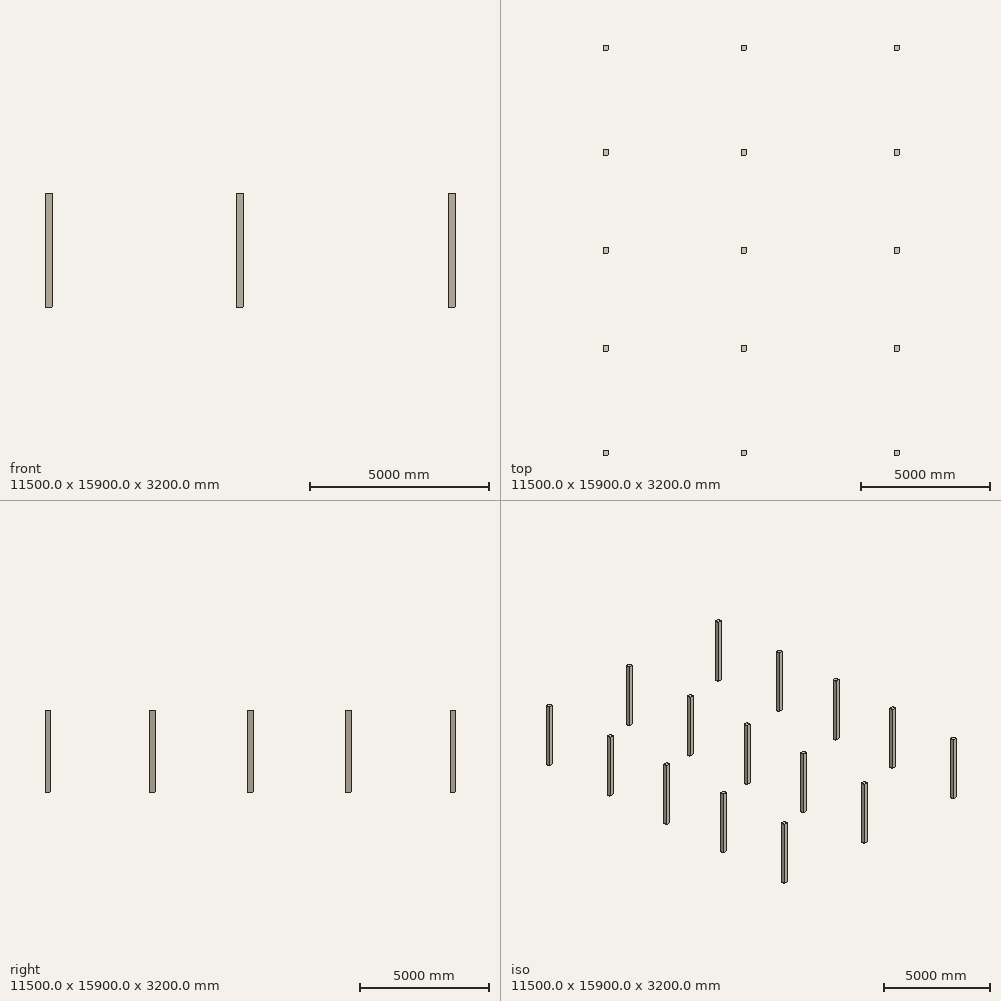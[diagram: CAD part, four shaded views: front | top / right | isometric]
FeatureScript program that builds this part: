
annotation { "Feature Type Name" : "Feature", "Feature Type Description" : "" }
export const myFeature = defineFeature(function(context is Context, id is Id, definition is map)
    precondition{}
    {
        {
            var Q0;
            Q0=qCreatedBy(makeId("Top.planeOp"),FACE);
            var sketch = newSketch(context, id + "F0", { "sketchPlane" : qUnion([Q0])});
            skLineSegment(sketch, "E0.bottom", {"start": v(5550, 7750) * mm, "end": v(-5550, 7750) * mm, "construction": true});
            skLineSegment(sketch, "E0.top", {"start": v(5550, -7750) * mm, "end": v(-5550, -7750) * mm, "construction": true});
            skLineSegment(sketch, "E0.left", {"start": v(5550, 7750) * mm, "end": v(5550, -7750) * mm, "construction": true});
            skLineSegment(sketch, "E0.right", {"start": v(-5550, 7750) * mm, "end": v(-5550, -7750) * mm, "construction": true});
            skPoint(sketch, "E0.middle", {"position": v(0, 0) * mm});
            skLineSegment(sketch, "E1", {"start": v(-300, -7750) * mm, "end": v(-300, 7750) * mm, "construction": true});
            skPoint(sketch, "E2", {"position": v(-5550, 0) * mm});
            skPoint(sketch, "E3", {"position": v(-5550, 3800) * mm});
            skPoint(sketch, "E4", {"position": v(-5550, -3800) * mm});
            skPoint(sketch, "E5", {"position": v(5550, -3800) * mm});
            skPoint(sketch, "E6", {"position": v(5550, 0) * mm});
            skPoint(sketch, "E7", {"position": v(5550, 3800) * mm});
            skLineSegment(sketch, "E8", {"start": v(900, 7750) * mm, "end": v(900, -7750) * mm, "construction": true});
            skLineSegment(sketch, "E9", {"start": v(5550, 3800) * mm, "end": v(900, 3800) * mm, "construction": true});
            skLineSegment(sketch, "E10", {"start": v(5550, 0) * mm, "end": v(900, 0) * mm, "construction": true});
            skLineSegment(sketch, "E11", {"start": v(5550, -3800) * mm, "end": v(900, -3800) * mm, "construction": true});
            skLineSegment(sketch, "E12", {"start": v(5550, 4900) * mm, "end": v(2550, 4900) * mm, "construction": true});
            skLineSegment(sketch, "E13", {"start": v(2550, 4900) * mm, "end": v(2550, 2700) * mm, "construction": true});
            skLineSegment(sketch, "E14", {"start": v(2550, -4900) * mm, "end": v(5550, -4900) * mm, "construction": true});
            skLineSegment(sketch, "E15", {"start": v(-4350, 7750) * mm, "end": v(-4350, 1750) * mm, "construction": true});
            skLineSegment(sketch, "E16", {"start": v(-4350, 1750) * mm, "end": v(-300, 1750) * mm, "construction": true});
            skLineSegment(sketch, "E17", {"start": v(-4350, 4750) * mm, "end": v(-3250, 4750) * mm, "construction": true});
            skLineSegment(sketch, "E18", {"start": v(-3250, 4750) * mm, "end": v(-3250, 7750) * mm, "construction": true});
            skLineSegment(sketch, "E19", {"start": v(-5550, 0) * mm, "end": v(-2550, 0) * mm, "construction": true});
            skLineSegment(sketch, "E20", {"start": v(-2550, 0) * mm, "end": v(-2550, -3800) * mm, "construction": true});
            skLineSegment(sketch, "E21", {"start": v(-2550, -3800) * mm, "end": v(-5550, -3800) * mm, "construction": true});
            skLineSegment(sketch, "E22", {"start": v(-5550, -2700) * mm, "end": v(-2550, -2700) * mm, "construction": true});
            skLineSegment(sketch, "E23", {"start": v(2550, 2700) * mm, "end": v(5550, 2700) * mm, "construction": true});
            skLineSegment(sketch, "E24", {"start": v(2550, -2700) * mm, "end": v(5550, -2700) * mm, "construction": true});
            skLineSegment(sketch, "E25.trimOffspring", {"start": v(2550, -2700) * mm, "end": v(2550, -4900) * mm, "construction": true});
            skPoint(sketch, "E26", {"position": v(-300, 0) * mm});
            skPoint(sketch, "E27", {"position": v(-300, 3800) * mm});
            skPoint(sketch, "E28", {"position": v(-300, -3800) * mm});
            skSolve(sketch);
        }
        {
            var Q0;
            Q0=qCreatedBy(makeId("Top.planeOp"),FACE);
            var sketch = newSketch(context, id + "F1", { "sketchPlane" : qUnion([Q0])});
            skLineSegment(sketch, "E29.0", {"start": v(5550, 7750) * mm, "end": v(-5550, 7750) * mm, "construction": true});
            skLineSegment(sketch, "E30.0", {"start": v(-5550, 7750) * mm, "end": v(-5550, -7750) * mm, "construction": true});
            skLineSegment(sketch, "E31.0", {"start": v(5550, -7750) * mm, "end": v(-5550, -7750) * mm, "construction": true});
            skLineSegment(sketch, "E32.0", {"start": v(5550, 7750) * mm, "end": v(5550, -7750) * mm, "construction": true});
            skLineSegment(sketch, "E33.0", {"start": v(5750, 7950) * mm, "end": v(-5750, 7950) * mm, "construction": true});
            skLineSegment(sketch, "E33.1", {"start": v(5750, 7950) * mm, "end": v(5750, -7950) * mm, "construction": true});
            skLineSegment(sketch, "E33.2", {"start": v(5750, -7950) * mm, "end": v(-5750, -7950) * mm, "construction": true});
            skLineSegment(sketch, "E33.3", {"start": v(-5750, 7950) * mm, "end": v(-5750, -7950) * mm, "construction": true});
            skLineSegment(sketch, "E34", {"start": v(-5750, -7950) * mm, "end": v(-5550, -7750) * mm, "construction": true});
            skLineSegment(sketch, "E35", {"start": v(5550, -7750) * mm, "end": v(5750, -7950) * mm, "construction": true});
            skLineSegment(sketch, "E36", {"start": v(5550, 7750) * mm, "end": v(5750, 7950) * mm, "construction": true});
            skLineSegment(sketch, "E37", {"start": v(-5550, 7750) * mm, "end": v(-5750, 7950) * mm, "construction": true});
            skPoint(sketch, "E38.0", {"position": v(-5550, 3800) * mm});
            skPoint(sketch, "E39.0", {"position": v(-300, 3800) * mm});
            skPoint(sketch, "E40.0", {"position": v(-300, 0) * mm});
            skPoint(sketch, "E41.0", {"position": v(5550, 0) * mm});
            skPoint(sketch, "E42.0", {"position": v(5550, 3800) * mm});
            skPoint(sketch, "E43.0", {"position": v(-300, 7750) * mm});
            skPoint(sketch, "E44.0", {"position": v(-5550, 0) * mm});
            skPoint(sketch, "E45.0", {"position": v(-5550, -3800) * mm});
            skPoint(sketch, "E46.0", {"position": v(-300, -3800) * mm});
            skPoint(sketch, "E47.0", {"position": v(5550, -3800) * mm});
            skPoint(sketch, "E48.0", {"position": v(-300, -7750) * mm});
            skLineSegment(sketch, "E49", {"start": v(-5550, -3800) * mm, "end": v(-5750, -3800) * mm, "construction": true});
            skLineSegment(sketch, "E50", {"start": v(-300, -7750) * mm, "end": v(-300, -7950) * mm, "construction": true});
            skPoint(sketch, "E51", {"position": v(-5650, -7850) * mm});
            skPoint(sketch, "E52", {"position": v(-300, -7850) * mm});
            skPoint(sketch, "E53", {"position": v(5650, -7850) * mm});
            skLineSegment(sketch, "E54", {"start": v(5550, -3800) * mm, "end": v(5750, -3800) * mm, "construction": true});
            skPoint(sketch, "E55", {"position": v(5650, -3800) * mm});
            skLineSegment(sketch, "E56", {"start": v(5550, 0) * mm, "end": v(5750, 0) * mm, "construction": true});
            skLineSegment(sketch, "E57", {"start": v(5550, 3800) * mm, "end": v(5750, 3800) * mm, "construction": true});
            skPoint(sketch, "E58", {"position": v(5650, 3800) * mm});
            skPoint(sketch, "E59", {"position": v(5650, 0) * mm});
            skPoint(sketch, "E60", {"position": v(5650, 7850) * mm});
            skLineSegment(sketch, "E61", {"start": v(-300, 7750) * mm, "end": v(-300, 7950) * mm, "construction": true});
            skPoint(sketch, "E62", {"position": v(-300, 7850) * mm});
            skPoint(sketch, "E63", {"position": v(-5650, 7850) * mm});
            skLineSegment(sketch, "E64", {"start": v(-5550, 3800) * mm, "end": v(-5750, 3800) * mm, "construction": true});
            skPoint(sketch, "E65", {"position": v(-5650, 3800) * mm});
            skPoint(sketch, "E66", {"position": v(-5650, -3800) * mm});
            skLineSegment(sketch, "E67", {"start": v(-5550, 0) * mm, "end": v(-5750, 0) * mm, "construction": true});
            skPoint(sketch, "E68", {"position": v(-5650, 0) * mm});
            skLineSegment(sketch, "E69.bottom", {"start": v(-5550, -7750) * mm, "end": v(-5750, -7750) * mm});
            skLineSegment(sketch, "E69.top", {"start": v(-5550, -7950) * mm, "end": v(-5750, -7950) * mm});
            skLineSegment(sketch, "E69.left", {"start": v(-5550, -7750) * mm, "end": v(-5550, -7950) * mm});
            skLineSegment(sketch, "E69.right", {"start": v(-5750, -7750) * mm, "end": v(-5750, -7950) * mm});
            skLineSegment(sketch, "E70.bottom", {"start": v(-200, -7750) * mm, "end": v(-400, -7750) * mm});
            skLineSegment(sketch, "E70.top", {"start": v(-200, -7950) * mm, "end": v(-400, -7950) * mm});
            skLineSegment(sketch, "E70.left", {"start": v(-200, -7750) * mm, "end": v(-200, -7950) * mm});
            skLineSegment(sketch, "E70.right", {"start": v(-400, -7750) * mm, "end": v(-400, -7950) * mm});
            skLineSegment(sketch, "E71.bottom", {"start": v(5750, -7750) * mm, "end": v(5550, -7750) * mm});
            skLineSegment(sketch, "E71.top", {"start": v(5750, -7950) * mm, "end": v(5550, -7950) * mm});
            skLineSegment(sketch, "E71.left", {"start": v(5750, -7750) * mm, "end": v(5750, -7950) * mm});
            skLineSegment(sketch, "E71.right", {"start": v(5550, -7750) * mm, "end": v(5550, -7950) * mm});
            skLineSegment(sketch, "E72.bottom", {"start": v(-5550, -3700) * mm, "end": v(-5750, -3700) * mm});
            skLineSegment(sketch, "E72.top", {"start": v(-5550, -3900) * mm, "end": v(-5750, -3900) * mm});
            skLineSegment(sketch, "E72.left", {"start": v(-5550, -3700) * mm, "end": v(-5550, -3900) * mm});
            skLineSegment(sketch, "E72.right", {"start": v(-5750, -3700) * mm, "end": v(-5750, -3900) * mm});
            skLineSegment(sketch, "E73.bottom", {"start": v(-400, -3700) * mm, "end": v(-200, -3700) * mm});
            skLineSegment(sketch, "E73.top", {"start": v(-400, -3900) * mm, "end": v(-200, -3900) * mm});
            skLineSegment(sketch, "E73.left", {"start": v(-400, -3700) * mm, "end": v(-400, -3900) * mm});
            skLineSegment(sketch, "E73.right", {"start": v(-200, -3700) * mm, "end": v(-200, -3900) * mm});
            skLineSegment(sketch, "E74.bottom", {"start": v(5750, -3700) * mm, "end": v(5550, -3700) * mm});
            skLineSegment(sketch, "E74.top", {"start": v(5750, -3900) * mm, "end": v(5550, -3900) * mm});
            skLineSegment(sketch, "E74.left", {"start": v(5750, -3700) * mm, "end": v(5750, -3900) * mm});
            skLineSegment(sketch, "E74.right", {"start": v(5550, -3700) * mm, "end": v(5550, -3900) * mm});
            skLineSegment(sketch, "E75.bottom", {"start": v(-5550, 100) * mm, "end": v(-5750, 100) * mm});
            skLineSegment(sketch, "E75.top", {"start": v(-5550, -100) * mm, "end": v(-5750, -100) * mm});
            skLineSegment(sketch, "E75.left", {"start": v(-5550, 100) * mm, "end": v(-5550, -100) * mm});
            skLineSegment(sketch, "E75.right", {"start": v(-5750, 100) * mm, "end": v(-5750, -100) * mm});
            skLineSegment(sketch, "E76.bottom", {"start": v(-200, 100) * mm, "end": v(-400, 100) * mm});
            skLineSegment(sketch, "E76.top", {"start": v(-200, -100) * mm, "end": v(-400, -100) * mm});
            skLineSegment(sketch, "E76.left", {"start": v(-200, 100) * mm, "end": v(-200, -100) * mm});
            skLineSegment(sketch, "E76.right", {"start": v(-400, 100) * mm, "end": v(-400, -100) * mm});
            skLineSegment(sketch, "E77.bottom", {"start": v(5550, -100) * mm, "end": v(5750, -100) * mm});
            skLineSegment(sketch, "E77.top", {"start": v(5550, 100) * mm, "end": v(5750, 100) * mm});
            skLineSegment(sketch, "E77.left", {"start": v(5550, -100) * mm, "end": v(5550, 100) * mm});
            skLineSegment(sketch, "E77.right", {"start": v(5750, -100) * mm, "end": v(5750, 100) * mm});
            skLineSegment(sketch, "E78.bottom", {"start": v(-5550, 3900) * mm, "end": v(-5750, 3900) * mm});
            skLineSegment(sketch, "E78.top", {"start": v(-5550, 3700) * mm, "end": v(-5750, 3700) * mm});
            skLineSegment(sketch, "E78.left", {"start": v(-5550, 3900) * mm, "end": v(-5550, 3700) * mm});
            skLineSegment(sketch, "E78.right", {"start": v(-5750, 3900) * mm, "end": v(-5750, 3700) * mm});
            skLineSegment(sketch, "E79.bottom", {"start": v(-200, 3900) * mm, "end": v(-400, 3900) * mm});
            skLineSegment(sketch, "E79.top", {"start": v(-200, 3700) * mm, "end": v(-400, 3700) * mm});
            skLineSegment(sketch, "E79.left", {"start": v(-200, 3900) * mm, "end": v(-200, 3700) * mm});
            skLineSegment(sketch, "E79.right", {"start": v(-400, 3900) * mm, "end": v(-400, 3700) * mm});
            skLineSegment(sketch, "E80.bottom", {"start": v(5750, 3900) * mm, "end": v(5550, 3900) * mm});
            skLineSegment(sketch, "E80.top", {"start": v(5750, 3700) * mm, "end": v(5550, 3700) * mm});
            skLineSegment(sketch, "E80.left", {"start": v(5750, 3900) * mm, "end": v(5750, 3700) * mm});
            skLineSegment(sketch, "E80.right", {"start": v(5550, 3900) * mm, "end": v(5550, 3700) * mm});
            skLineSegment(sketch, "E81.bottom", {"start": v(-5550, 7950) * mm, "end": v(-5750, 7950) * mm});
            skLineSegment(sketch, "E81.top", {"start": v(-5550, 7750) * mm, "end": v(-5750, 7750) * mm});
            skLineSegment(sketch, "E81.left", {"start": v(-5550, 7950) * mm, "end": v(-5550, 7750) * mm});
            skLineSegment(sketch, "E81.right", {"start": v(-5750, 7950) * mm, "end": v(-5750, 7750) * mm});
            skLineSegment(sketch, "E82.bottom", {"start": v(-400, 7950) * mm, "end": v(-200, 7950) * mm});
            skLineSegment(sketch, "E82.top", {"start": v(-400, 7750) * mm, "end": v(-200, 7750) * mm});
            skLineSegment(sketch, "E82.left", {"start": v(-400, 7950) * mm, "end": v(-400, 7750) * mm});
            skLineSegment(sketch, "E82.right", {"start": v(-200, 7950) * mm, "end": v(-200, 7750) * mm});
            skLineSegment(sketch, "E83.bottom", {"start": v(5750, 7950) * mm, "end": v(5550, 7950) * mm});
            skLineSegment(sketch, "E83.top", {"start": v(5750, 7750) * mm, "end": v(5550, 7750) * mm});
            skLineSegment(sketch, "E83.left", {"start": v(5750, 7950) * mm, "end": v(5750, 7750) * mm});
            skLineSegment(sketch, "E83.right", {"start": v(5550, 7950) * mm, "end": v(5550, 7750) * mm});
            skSolve(sketch);
        }
        {
            var Q0;
            Q0 = qSketchRegion(id + "F1", true);
            extrude(context, id + "F2", {"entities" : qUnion([Q0]), "depth" : 3000 * mm + 200 * mm});
        }
    });
